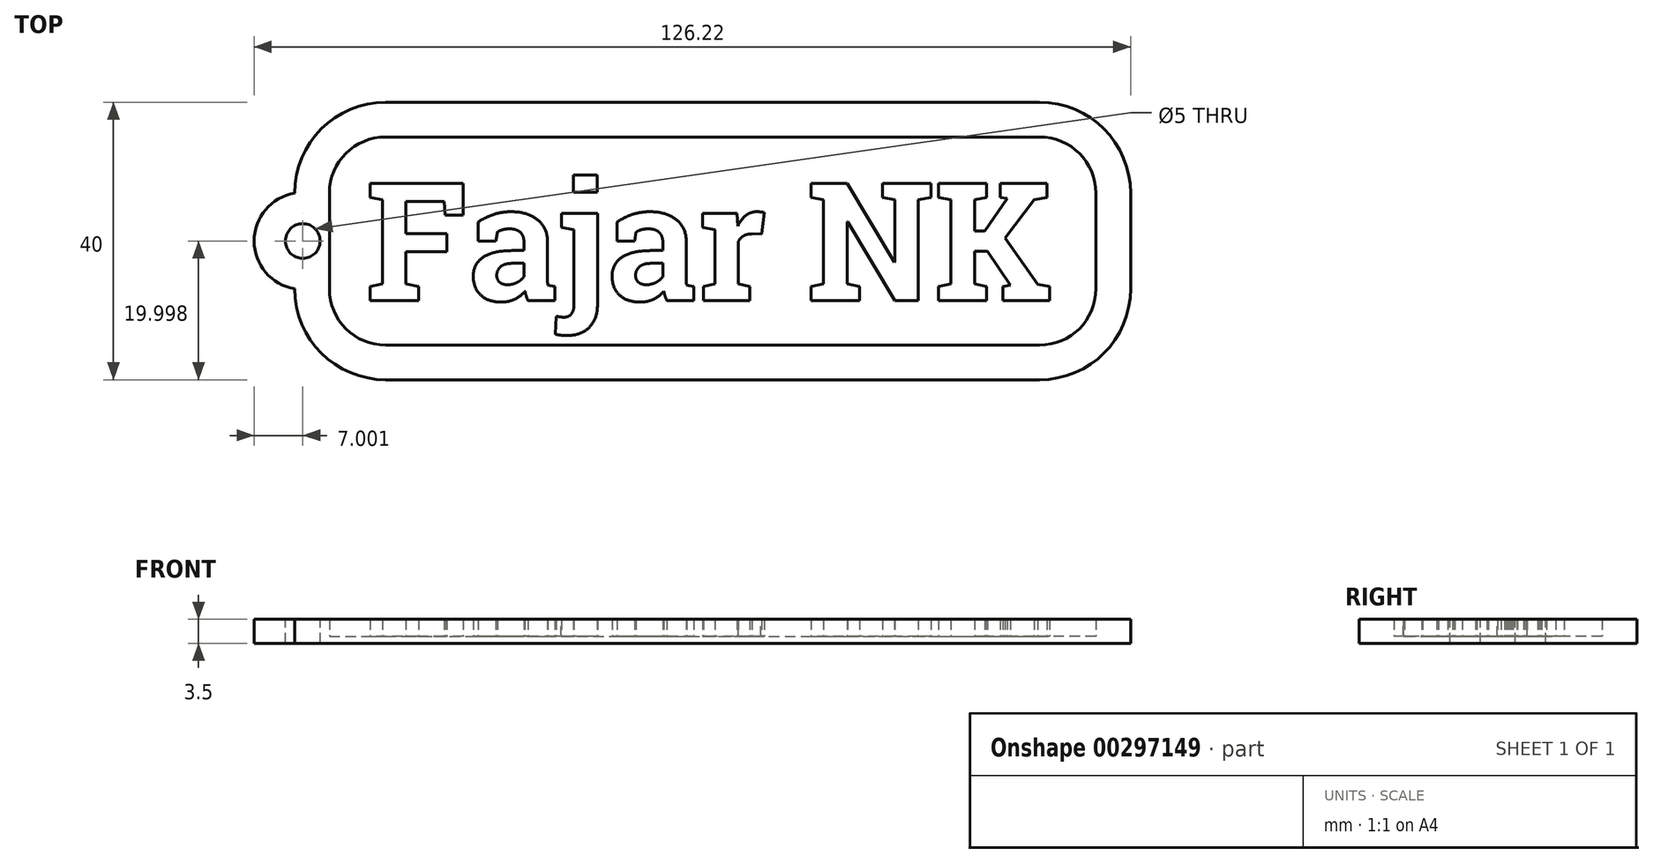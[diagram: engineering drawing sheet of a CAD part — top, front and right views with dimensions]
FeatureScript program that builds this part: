
annotation { "Feature Type Name" : "Feature", "Feature Type Description" : "" }
export const myFeature = defineFeature(function(context is Context, id is Id, definition is map)
    precondition{}
    {
        {
            var Q0;
            Q0=qCreatedBy(makeId("Top.planeOp"),FACE);
            var sketch = newSketch(context, id + "F0", { "sketchPlane" : qUnion([Q0])});
            skLineSegment(sketch, "E0.bottom", {"start": v(-19.05, 12.4) * mm, "end": v(75.13, 12.4) * mm});
            skLineSegment(sketch, "E0.top", {"start": v(-19.05, -17.6) * mm, "end": v(75.13, -17.6) * mm});
            skLineSegment(sketch, "E0.left", {"start": v(-27.15, 4.3) * mm, "end": v(-27.15, -9.5) * mm});
            skLineSegment(sketch, "E0.right", {"start": v(83.23, 4.3) * mm, "end": v(83.23, -9.5) * mm});
            skPoint(sketch, "E1.visualSharp", {"position": v(-27.15, 12.4) * mm});
            skArc(sketch, "E1.filletArc", {"start": v(-19.05, 12.4) * mm, "mid": v(-24.78, 10.03) * mm, "end": v(-27.15, 4.3) * mm});
            skPoint(sketch, "E2.visualSharp", {"position": v(-27.15, -17.6) * mm});
            skArc(sketch, "E2.filletArc", {"start": v(-27.15, -9.5) * mm, "mid": v(-24.78, -15.23) * mm, "end": v(-19.05, -17.6) * mm});
            skPoint(sketch, "E3.visualSharp", {"position": v(83.23, -17.6) * mm});
            skArc(sketch, "E3.filletArc", {"start": v(75.13, -17.6) * mm, "mid": v(80.85, -15.23) * mm, "end": v(83.23, -9.5) * mm});
            skPoint(sketch, "E4.visualSharp", {"position": v(83.23, 12.4) * mm});
            skArc(sketch, "E4.filletArc", {"start": v(83.23, 4.3) * mm, "mid": v(80.85, 10.03) * mm, "end": v(75.13, 12.4) * mm});
            skArc(sketch, "E5.0", {"start": v(-19.05, 17.4) * mm, "mid": v(-28.31, 13.56) * mm, "end": v(-32.15, 4.3) * mm});
            skLineSegment(sketch, "E5.1", {"start": v(-32.15, 4.3) * mm, "end": v(-32.15, -9.5) * mm, "construction": true});
            skLineSegment(sketch, "E5.2", {"start": v(-19.05, 17.4) * mm, "end": v(75.13, 17.4) * mm});
            skArc(sketch, "E5.3", {"start": v(-32.15, -9.5) * mm, "mid": v(-28.31, -18.77) * mm, "end": v(-19.05, -22.6) * mm});
            skArc(sketch, "E5.4", {"start": v(88.23, 4.3) * mm, "mid": v(84.39, 13.56) * mm, "end": v(75.13, 17.4) * mm});
            skLineSegment(sketch, "E5.5", {"start": v(88.23, 4.3) * mm, "end": v(88.23, -9.5) * mm});
            skArc(sketch, "E5.6", {"start": v(75.13, -22.6) * mm, "mid": v(84.39, -18.77) * mm, "end": v(88.23, -9.5) * mm});
            skLineSegment(sketch, "E5.7", {"start": v(-19.05, -22.6) * mm, "end": v(75.13, -22.6) * mm});
            skArc(sketch, "E6", {"start": v(-32.15, 4.3) * mm, "mid": v(-37.99, -2.6) * mm, "end": v(-32.15, -9.5) * mm});
            skCircle(sketch, "E7", {"center": v(-30.99, -2.6) * mm, "radius": 2.5 * mm});
            skSolve(sketch);
        }
        {
            var Q0;
            Q0=makeQuery(id+"F0.imprint","IMPRINT",FACE,{"disambiguationData":[TD([[makeQuery(id+"F0.imprint","IMPRINT",EDGE,{"derivedFrom":sQuery(id+"F0.wireOp",EDGE,"E0.bottom")}),1.0]])]});
            var Q1;
            Q1=makeQuery(id+"F0.imprint","IMPRINT",FACE,{"disambiguationData":[TD([[makeQuery(id+"F0.imprint","IMPRINT",EDGE,{"derivedFrom":sQuery(id+"F0.wireOp",EDGE,"E0.bottom")}),-1.0]])]});
            extrude(context, id + "F1", {"entities" : qUnion([Q0, Q1]), "oppositeDirection" : true, "depth" : 1 * mm});
        }
        {
            var Q0;
            Q0=qCreatedBy(makeId("Top.planeOp"),FACE);
            var sketch = newSketch(context, id + "F2", { "sketchPlane" : qUnion([Q0])});
            skText(sketch, "E8", { "text": "Fajar NK", "fontName": "RobotoSlab-Bold.ttf"});
            skLineSegment(sketch, "E9", {"start": v(-21.96, -2.6) * mm, "end": v(-30.99, -2.6) * mm, "construction": true});
            skPoint(sketch, "E10.0", {"position": v(-30.99, -2.6) * mm});
            skLineSegment(sketch, "E11", {"start": v(28.04, 5.95) * mm, "end": v(28.04, 12.4) * mm});
            skPoint(sketch, "E12.0", {"position": v(28.04, 12.4) * mm});
            const initialGuessF2  = {"E8": [-0.02196, -0.01116, 1, 0, 0.0171]};
            skSetInitialGuess(sketch, initialGuessF2);
            skSolve(sketch);
        }
        {
            var Q0;
            Q0=makeQuery(id+"F0.imprint","IMPRINT",FACE,{"disambiguationData":[TD([[makeQuery(id+"F0.imprint","IMPRINT",EDGE,{"derivedFrom":sQuery(id+"F0.wireOp",EDGE,"E0.bottom")}),1.0]])]});
            extrude(context, id + "F3", {"entities" : qUnion([Q0]), "operationType" : NewBodyOperationType.ADD, "depth" : 2.5 * mm});
        }
        {
            var Q0;
            Q0 = qSketchRegion(id + "F2", true);
            var Q1;
            Q1=makeQuery(id+"F3.opExtrude","CAP_FACE",FACE,{"disambiguationData":[OSD([sQuery(id+"F0.wireOp",EDGE,"E0.bottom"),sQuery(id+"F0.wireOp",EDGE,"E0.top"),sQuery(id+"F0.wireOp",EDGE,"E0.left"),sQuery(id+"F0.wireOp",EDGE,"E0.right"),sQuery(id+"F0.wireOp",EDGE,"E1.filletArc"),sQuery(id+"F0.wireOp",EDGE,"E2.filletArc"),sQuery(id+"F0.wireOp",EDGE,"E3.filletArc"),sQuery(id+"F0.wireOp",EDGE,"E4.filletArc"),sQuery(id+"F0.wireOp",EDGE,"E5.0"),sQuery(id+"F0.wireOp",EDGE,"E5.2"),sQuery(id+"F0.wireOp",EDGE,"E5.3"),sQuery(id+"F0.wireOp",EDGE,"E5.4"),sQuery(id+"F0.wireOp",EDGE,"E5.5"),sQuery(id+"F0.wireOp",EDGE,"E5.6"),sQuery(id+"F0.wireOp",EDGE,"E5.7"),sQuery(id+"F0.wireOp",EDGE,"E6"),sQuery(id+"F0.wireOp",EDGE,"E7")])],"isStart":false});
            extrude(context, id + "F4", {"entities" : qUnion([Q0]), "operationType" : NewBodyOperationType.ADD, "endBound" : BoundingType.UP_TO_SURFACE, "endBoundEntityFace" : qUnion([Q1]), "depth" : 3 * mm});
        }
    });
